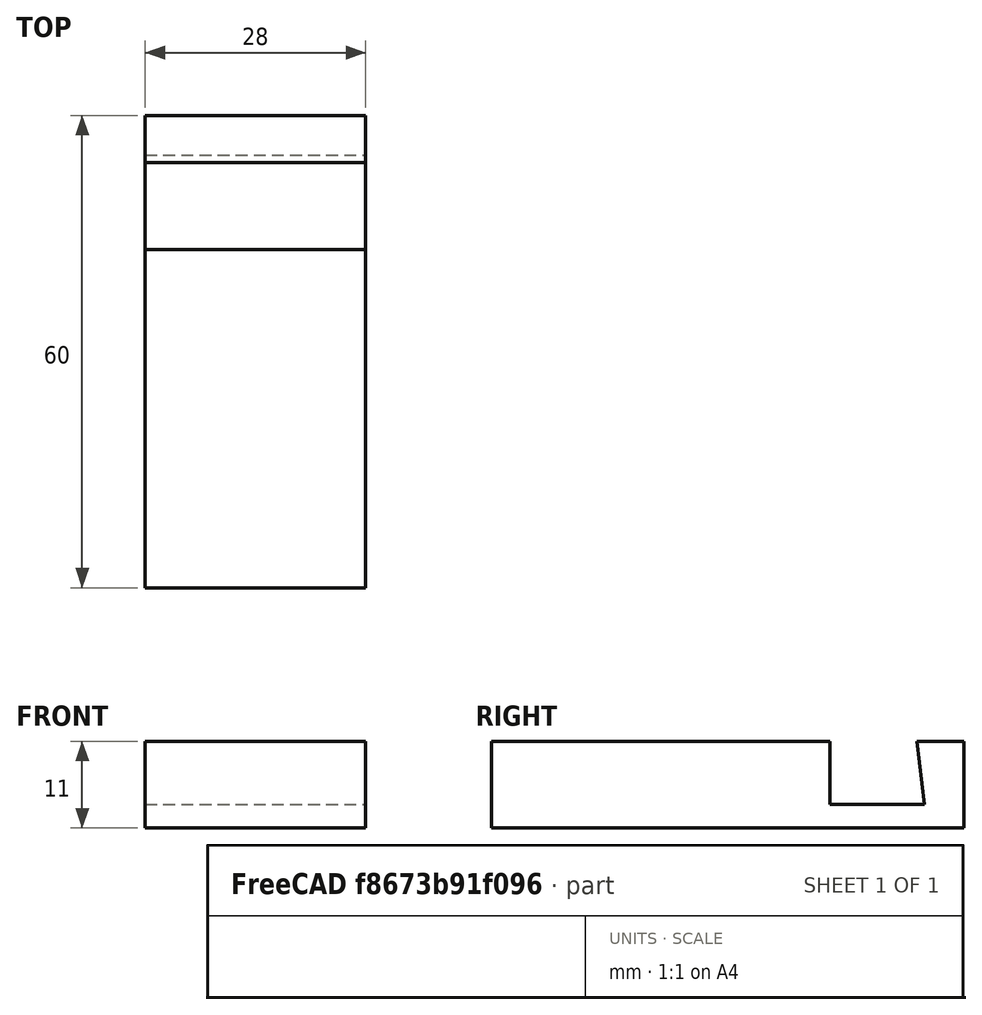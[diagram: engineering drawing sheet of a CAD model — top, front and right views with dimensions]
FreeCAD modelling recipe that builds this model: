
FCSTD DOCUMENT  (FreeCAD 0.16R6707 (Git))
Label: 02-porta-moviles-param
License: All rights reserved
LicenseURL: http://en.wikipedia.org/wiki/All_rights_reserved
objects: Sketcher::SketchObject×1, PartDesign::Pad×1, Spreadsheet::Sheet×1
note: 3 computed .brp shape members not serialized (recipe doc carries the construction recipe); baked Part::Feature solids carry a one-line shape summary decoded from their .brp

FEATURE [Sketcher::SketchObject] Sketch
  Placement = pos=(0,0,0) rot=(0.57735,0.57735,0.57735;2.0944rad)
  expr: Constraints[13] = param.alto
  expr: Constraints[14] = param.largo
  expr: Constraints[15] = param.em
  sketch-geometry (8):
    g0: LineSegment StartX=0 StartY=11 StartZ=0 EndX=0 EndY=0 EndZ=0
    g1: LineSegment StartX=0 StartY=0 StartZ=0 EndX=60 EndY=0 EndZ=0
    g2: LineSegment StartX=60 StartY=0 StartZ=0 EndX=60 EndY=11 EndZ=0
    g3: LineSegment StartX=60 StartY=11 StartZ=0 EndX=54 EndY=11 EndZ=0
    g4: LineSegment StartX=54 StartY=11 StartZ=0 EndX=54.9823 EndY=3 EndZ=0
    g5: LineSegment StartX=54.9823 StartY=3 StartZ=0 EndX=43 EndY=3 EndZ=0
    g6: LineSegment StartX=43 StartY=3 StartZ=0 EndX=43 EndY=11 EndZ=0
    g7: LineSegment StartX=43 StartY=11 StartZ=0 EndX=0 EndY=11 EndZ=0
  constraints (23):
    c: Vertical(g0)
    c: Coincident(g0,g1)
    c: Horizontal(g1)
    c: Coincident(g1,g2)
    c: Coincident(g2,g3)
    c: Coincident(g3,g4)
    c: Coincident(g4,g5)
    c: Horizontal(g5)
    c: Coincident(g5,g6)
    c: Vertical(g6)
    c: Coincident(g6,g7)
    c: Coincident(g7,g0)
    c: Horizontal(g7)
    c: DistanceY(g0,g0) = 11
    c: DistanceX(g1,g1) = 60
    c: DistanceX(g6,g3) = 11
    c: Vertical(g2)
    c: Horizontal(g3)
    c: Equal(g2,g0)
    c: DistanceY(g1,g4) = 3
    c: Coincident(g0,g-1)
    c: DistanceX(g3,g2) = 6
    c: Angle(g4,g5) = 1.44862
FEATURE [PartDesign::Pad] Pad
  Length = 28
  Length2 = 100
  Midplane = true
  Placement = pos=(0,0,0) rot=(0.57735,0.57735,0.57735;2.0944rad)
  Sketch = -> Sketch
  Type = 0
  expr: Length = param.ancho
FEATURE [Spreadsheet::Sheet] Spreadsheet  label="param"
  cells = B3=Alto; C3(alto)=11; D3=11; B4=Ancho; C4(ancho)=28; D4=28; B5=Largo; C5(largo)=60; D5=60; B6=Espesor movil; C6(em)=11; D6=11
